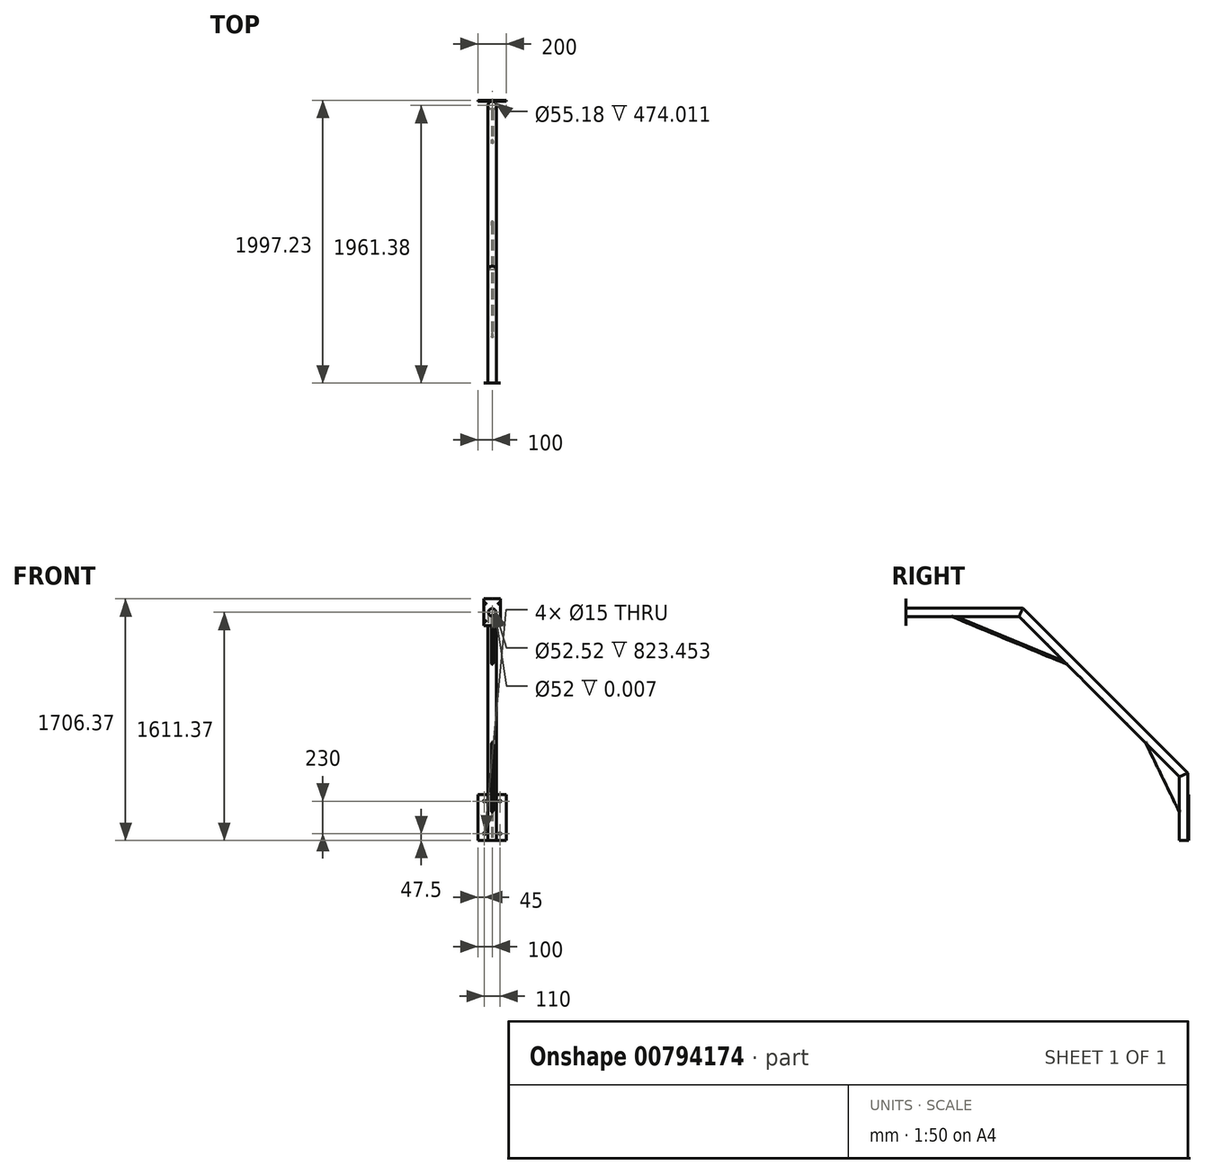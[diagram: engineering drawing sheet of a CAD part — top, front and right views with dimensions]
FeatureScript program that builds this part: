
annotation { "Feature Type Name" : "Feature", "Feature Type Description" : "" }
export const myFeature = defineFeature(function(context is Context, id is Id, definition is map)
    precondition{}
    {
        {
            var Q0;
            Q0=qCreatedBy(makeId("Top.planeOp"),FACE);
            var sketch = newSketch(context, id + "F0", { "sketchPlane" : qUnion([Q0])});
            skCircle(sketch, "E0", {"center": v(0, 0) * mm, "radius": 30 * mm});
            skCircle(sketch, "E1.0", {"center": v(0, 0) * mm, "radius": 27.59 * mm});
            skSolve(sketch);
        }
        {
            var Q0;
            Q0 = qSketchRegion(id + "F0", true);
            extrude(context, id + "F1", {"entities" : qUnion([Q0]), "depth" : 450 * mm, "offsetDistance" : 25 * mm});
        }
        {
            var Q0;
            Q0=qCreatedBy(makeId("Right.planeOp"),FACE);
            var sketch = newSketch(context, id + "F2", { "sketchPlane" : qUnion([Q0])});
            skLineSegment(sketch, "E2", {"start": v(-30, 450) * mm, "end": v(30, 510) * mm});
            skLineSegment(sketch, "E3.0", {"start": v(-30, 450) * mm, "end": v(30, 450) * mm, "construction": true});
            skSolve(sketch);
        }
        {
            var Q0;
            Q0=sQuery(id+"F2.wireOp",EDGE,"E2");
            var Q1;
            Q1=qCreatedBy(makeId("Top.planeOp"),FACE);
            cPlane(context, id + "F3", {"entities" : qUnion([Q0, Q1]), "cplaneType" : CPlaneType.LINE_ANGLE, "offset" : 25 * mm, "angle" : 0 * degree, "width" : 150 * mm, "height" : 150 * mm});
        }
        {
            var Q0;
            Q0=qCreatedBy(id+"F3.planeOp",FACE);
            var sketch = newSketch(context, id + "F4", { "sketchPlane" : qUnion([Q0])});
            skCircle(sketch, "E4", {"center": v(0, 326.98) * mm, "radius": 30 * mm});
            skCircle(sketch, "E5.0", {"center": v(0, 326.98) * mm, "radius": 26.26 * mm});
            skSolve(sketch);
        }
        {
            var Q0;
            Q0 = qSketchRegion(id + "F4", true);
            extrude(context, id + "F5", {"entities" : qUnion([Q0]), "operationType" : NewBodyOperationType.ADD, "oppositeDirection" : true, "depth" : 1600 * mm, "offsetDistance" : 25 * mm});
        }
        {
            var Q0;
            Q0=qCreatedBy(id+"F3.planeOp",FACE);
            var Q1;
            Q1=makeQuery(id+"F1.opExtrude","CAP_FACE",FACE,{"disambiguationData":[OSD([sQuery(id+"F0.wireOp",EDGE,"E0"),sQuery(id+"F0.wireOp",EDGE,"E1.0")])],"isStart":false});
            cPlane(context, id + "F6", {"entities" : qUnion([Q0, Q1]), "cplaneType" : CPlaneType.MID_PLANE, "offset" : 25 * mm, "width" : 150 * mm, "height" : 150 * mm});
        }
        {
            var Q0;
            Q0=makeQuery(id+"F5.opExtrude","CAP_FACE",FACE,{"disambiguationData":[OSD([sQuery(id+"F4.wireOp",EDGE,"E4"),sQuery(id+"F4.wireOp",EDGE,"E5.0")])],"isStart":true});
            var Q1;
            Q1=qCreatedBy(id+"F6.planeOp",FACE);
            extrude(context, id + "F7", {"entities" : qUnion([Q0]), "operationType" : NewBodyOperationType.ADD, "endBound" : BoundingType.UP_TO_SURFACE, "depth" : 25 * mm, "endBoundEntityFace" : qUnion([Q1]), "offsetDistance" : 25 * mm});
        }
        {
            var Q0;
            Q0=makeQuery(id+"F1.opExtrude","CAP_FACE",FACE,{"disambiguationData":[OSD([sQuery(id+"F0.wireOp",EDGE,"E0"),sQuery(id+"F0.wireOp",EDGE,"E1.0")])],"isStart":false});
            var Q1;
            Q1=qCreatedBy(id+"F6.planeOp",FACE);
            extrude(context, id + "F8", {"entities" : qUnion([Q0]), "operationType" : NewBodyOperationType.ADD, "endBound" : BoundingType.UP_TO_SURFACE, "depth" : 25 * mm, "endBoundEntityFace" : qUnion([Q1]), "offsetDistance" : 25 * mm});
        }
        {
            var Q0;
            Q0=qCreatedBy(makeId("Right.planeOp"),FACE);
            var sketch = newSketch(context, id + "F9", { "sketchPlane" : qUnion([Q0])});
            skLineSegment(sketch, "E6.0", {"start": v(-1118.94, 1623.8) * mm, "end": v(-1161.37, 1581.37) * mm, "construction": true});
            skLineSegment(sketch, "E7", {"start": v(-1161.37, 1581.37) * mm, "end": v(-1161.37, 1623.8) * mm, "construction": true});
            skSolve(sketch);
        }
        {
            var Q0;
            Q0=sQuery(id+"F9.wireOp",EDGE,"E7");
            var Q1;
            Q1=qCreatedBy(id+"F6.planeOp",FACE);
            cPlane(context, id + "F10", {"entities" : qUnion([Q0, Q1]), "cplaneType" : CPlaneType.LINE_ANGLE, "offset" : 25 * mm, "angle" : 0 * degree, "width" : 150 * mm, "height" : 150 * mm});
        }
        {
            var Q0;
            Q0=qCreatedBy(id+"F10.planeOp",FACE);
            var sketch = newSketch(context, id + "F11", { "sketchPlane" : qUnion([Q0])});
            skCircle(sketch, "E8", {"center": v(0, 1611.37) * mm, "radius": 30 * mm});
            skCircle(sketch, "E9.0", {"center": v(0, 1611.37) * mm, "radius": 26.26 * mm});
            skSolve(sketch);
        }
        {
            var Q0;
            Q0 = qSketchRegion(id + "F11", true);
            extrude(context, id + "F12", {"entities" : qUnion([Q0]), "depth" : 800 * mm, "offsetDistance" : 25 * mm});
        }
        {
            var Q0;
            Q0=makeQuery(id+"F12.opExtrude","CAP_FACE",FACE,{"disambiguationData":[OSD([sQuery(id+"F11.wireOp",EDGE,"E8"),sQuery(id+"F11.wireOp",EDGE,"E9.0")])],"isStart":true});
            var Q1;
            Q1=makeQuery(id+"F5.opExtrude","CAP_FACE",FACE,{"disambiguationData":[OSD([sQuery(id+"F4.wireOp",EDGE,"E4"),sQuery(id+"F4.wireOp",EDGE,"E5.0")])],"isStart":false});
            cPlane(context, id + "F13", {"entities" : qUnion([Q0, Q1]), "cplaneType" : CPlaneType.MID_PLANE, "offset" : 25 * mm, "width" : 150 * mm, "height" : 150 * mm});
        }
        {
            var Q0;
            Q0=makeQuery(id+"F5.opExtrude","CAP_FACE",FACE,{"disambiguationData":[OSD([sQuery(id+"F4.wireOp",EDGE,"E4"),sQuery(id+"F4.wireOp",EDGE,"E5.0")])],"isStart":false});
            var Q1;
            Q1=qCreatedBy(id+"F13.planeOp",FACE);
            extrude(context, id + "F14", {"entities" : qUnion([Q0]), "operationType" : NewBodyOperationType.ADD, "endBound" : BoundingType.UP_TO_SURFACE, "depth" : 25 * mm, "endBoundEntityFace" : qUnion([Q1]), "offsetDistance" : 25 * mm});
        }
        {
            var Q0;
            Q0=makeQuery(id+"F12.opExtrude","CAP_FACE",FACE,{"disambiguationData":[OSD([sQuery(id+"F11.wireOp",EDGE,"E8"),sQuery(id+"F11.wireOp",EDGE,"E9.0")])],"isStart":true});
            var Q1;
            Q1=qCreatedBy(id+"F13.planeOp",FACE);
            extrude(context, id + "F15", {"entities" : qUnion([Q0]), "operationType" : NewBodyOperationType.ADD, "endBound" : BoundingType.UP_TO_SURFACE, "depth" : 25 * mm, "endBoundEntityFace" : qUnion([Q1]), "offsetDistance" : 25 * mm});
        }
        {
            var Q0;
            Q0=makeQuery(id+"F12.opExtrude","CAP_FACE",FACE,{"disambiguationData":[OSD([sQuery(id+"F11.wireOp",EDGE,"E8"),sQuery(id+"F11.wireOp",EDGE,"E9.0")])],"isStart":false});
            var sketch = newSketch(context, id + "F16", { "sketchPlane" : qUnion([Q0])});
            skLineSegment(sketch, "E10.bottom", {"start": v(60, 1516.37) * mm, "end": v(-60, 1516.37) * mm});
            skLineSegment(sketch, "E10.top", {"start": v(60, 1706.37) * mm, "end": v(-60, 1706.37) * mm});
            skLineSegment(sketch, "E10.left", {"start": v(60, 1516.37) * mm, "end": v(60, 1706.37) * mm});
            skLineSegment(sketch, "E10.right", {"start": v(-60, 1516.37) * mm, "end": v(-60, 1706.37) * mm});
            skPoint(sketch, "E10.middle", {"position": v(0, 1611.37) * mm});
            skLineSegment(sketch, "E11.bottom", {"start": v(48, 1549.37) * mm, "end": v(-48, 1549.37) * mm, "construction": true});
            skLineSegment(sketch, "E11.top", {"start": v(48, 1673.37) * mm, "end": v(-48, 1673.37) * mm, "construction": true});
            skLineSegment(sketch, "E11.left", {"start": v(48, 1549.37) * mm, "end": v(48, 1673.37) * mm, "construction": true});
            skLineSegment(sketch, "E11.right", {"start": v(-48, 1549.37) * mm, "end": v(-48, 1673.37) * mm, "construction": true});
            skCircle(sketch, "E12", {"center": v(48, 1673.37) * mm, "radius": 4.5 * mm});
            skCircle(sketch, "E13", {"center": v(-48, 1673.37) * mm, "radius": 4.5 * mm});
            skCircle(sketch, "E14", {"center": v(48, 1549.37) * mm, "radius": 4.5 * mm});
            skCircle(sketch, "E15", {"center": v(-48, 1549.37) * mm, "radius": 4.5 * mm});
            skCircle(sketch, "E16", {"center": v(0, 1611.37) * mm, "radius": 26 * mm});
            skSolve(sketch);
        }
        {
            var Q0;
            Q0 = qSketchRegion(id + "F16", true);
            extrude(context, id + "F17", {"entities" : qUnion([Q0]), "operationType" : NewBodyOperationType.ADD, "depth" : 3 / 406.4 * mm, "offsetDistance" : 25 * mm});
        }
        {
            var Q0;
            Q0=qCreatedBy(makeId("Right.planeOp"),FACE);
            var sketch = newSketch(context, id + "F18", { "sketchPlane" : qUnion([Q0])});
            skLineSegment(sketch, "E17.bottom", {"start": v(29.5, 325) * mm, "end": v(35.85, 325) * mm});
            skLineSegment(sketch, "E17.top", {"start": v(29.5, 0) * mm, "end": v(35.85, 0) * mm});
            skLineSegment(sketch, "E17.left", {"start": v(29.5, 325) * mm, "end": v(29.5, 0) * mm});
            skLineSegment(sketch, "E17.right", {"start": v(35.85, 325) * mm, "end": v(35.85, 0) * mm});
            skSolve(sketch);
        }
        {
            var Q0;
            Q0 = qSketchRegion(id + "F18", true);
            extrude(context, id + "F19", {"entities" : qUnion([Q0]), "operationType" : NewBodyOperationType.ADD, "endBound" : BoundingType.SYMMETRIC, "depth" : 200 * mm, "offsetDistance" : 25 * mm});
        }
        {
            var Q0;
            Q0=makeQuery(id+"F19.opExtrude","SWEPT_FACE",FACE,{"disambiguationData":[OSD([sQuery(id+"F18.wireOp",EDGE,"E17.right")])]});
            var sketch = newSketch(context, id + "F20", { "sketchPlane" : qUnion([Q0])});
            skCircle(sketch, "E18", {"center": v(-55, 277.5) * mm, "radius": 7.5 * mm});
            skLineSegment(sketch, "E19.bottom", {"start": v(55, 47.5) * mm, "end": v(-55, 47.5) * mm, "construction": true});
            skLineSegment(sketch, "E19.top", {"start": v(55, 277.5) * mm, "end": v(-55, 277.5) * mm, "construction": true});
            skLineSegment(sketch, "E19.left", {"start": v(55, 47.5) * mm, "end": v(55, 277.5) * mm, "construction": true});
            skLineSegment(sketch, "E19.right", {"start": v(-55, 47.5) * mm, "end": v(-55, 277.5) * mm, "construction": true});
            skPoint(sketch, "E19.middle", {"position": v(0, 162.5) * mm});
            skPoint(sketch, "E19.middle.positionSnap0", {"position": v(0, 325) * mm});
            skPoint(sketch, "E19.middle.positionSnap1", {"position": v(100, 162.5) * mm});
            skPoint(sketch, "E19.centerSnap0", {"position": v(0, 325) * mm});
            skPoint(sketch, "E19.centerSnap1", {"position": v(100, 162.5) * mm});
            skCircle(sketch, "E20", {"center": v(55, 277.5) * mm, "radius": 7.5 * mm});
            skCircle(sketch, "E21", {"center": v(55, 47.5) * mm, "radius": 7.5 * mm});
            skCircle(sketch, "E22", {"center": v(-55, 47.5) * mm, "radius": 7.5 * mm});
            skSolve(sketch);
        }
        {
            var Q0;
            Q0 = qSketchRegion(id + "F20", true);
            extrude(context, id + "F21", {"entities" : qUnion([Q0]), "operationType" : NewBodyOperationType.REMOVE, "endBound" : BoundingType.UP_TO_NEXT, "oppositeDirection" : true, "depth" : 25 * mm, "offsetDistance" : 25 * mm});
        }
        {
            var Q0;
            Q0=qCreatedBy(makeId("Right.planeOp"),FACE);
            var sketch = newSketch(context, id + "F22", { "sketchPlane" : qUnion([Q0])});
            skLineSegment(sketch, "E23", {"start": v(-1621.37, 1581.37) * mm, "end": v(-833.88, 1255.18) * mm});
            skLineSegment(sketch, "E24", {"start": v(-1621.37, 1581.37) * mm, "end": v(-778.17, 1581.37) * mm, "construction": true});
            skLineSegment(sketch, "E25.0", {"start": v(-1637.96, 1581.37) * mm, "end": v(-822.56, 1243.62) * mm});
            skLineSegment(sketch, "E26", {"start": v(-1621.37, 1581.37) * mm, "end": v(-1637.96, 1581.37) * mm});
            skLineSegment(sketch, "E27", {"start": v(-833.88, 1255.18) * mm, "end": v(-822.56, 1243.62) * mm});
            skSolve(sketch);
        }
        {
            var Q0;
            Q0 = qSketchRegion(id + "F22", true);
            var Q1;
            Q1=sQuery(id+"F22.wireOp",EDGE,"E23");
            revolve(context, id + "F23", {"operationType" : NewBodyOperationType.ADD, "surfaceOperationType" : NewSurfaceOperationType.NEW, "entities" : qUnion([Q0]), "axis" : qUnion([Q1]), "revolveType" : RevolveType.FULL});
        }
        {
            var Q0;
            Q0=qCreatedBy(makeId("Right.planeOp"),FACE);
            var sketch = newSketch(context, id + "F24", { "sketchPlane" : qUnion([Q0])});
            skLineSegment(sketch, "E28", {"start": v(0, 0) * mm, "end": v(0, 590.25) * mm, "construction": true});
            skLineSegment(sketch, "E29", {"start": v(-257.09, 680.6) * mm, "end": v(-30, 215) * mm});
            skLineSegment(sketch, "E30.0", {"start": v(-269.91, 692.4) * mm, "end": v(-30.03, 200.58) * mm});
            skLineSegment(sketch, "E31", {"start": v(-269.91, 692.4) * mm, "end": v(-257.09, 680.6) * mm});
            skLineSegment(sketch, "E32", {"start": v(-30, 215) * mm, "end": v(-30.03, 200.58) * mm});
            skSolve(sketch);
        }
        {
            var Q0;
            Q0 = qSketchRegion(id + "F24", true);
            var Q1;
            Q1=sQuery(id+"F24.wireOp",EDGE,"E29");
            revolve(context, id + "F25", {"operationType" : NewBodyOperationType.ADD, "surfaceOperationType" : NewSurfaceOperationType.NEW, "entities" : qUnion([Q0]), "axis" : qUnion([Q1]), "revolveType" : RevolveType.FULL});
        }
    });
